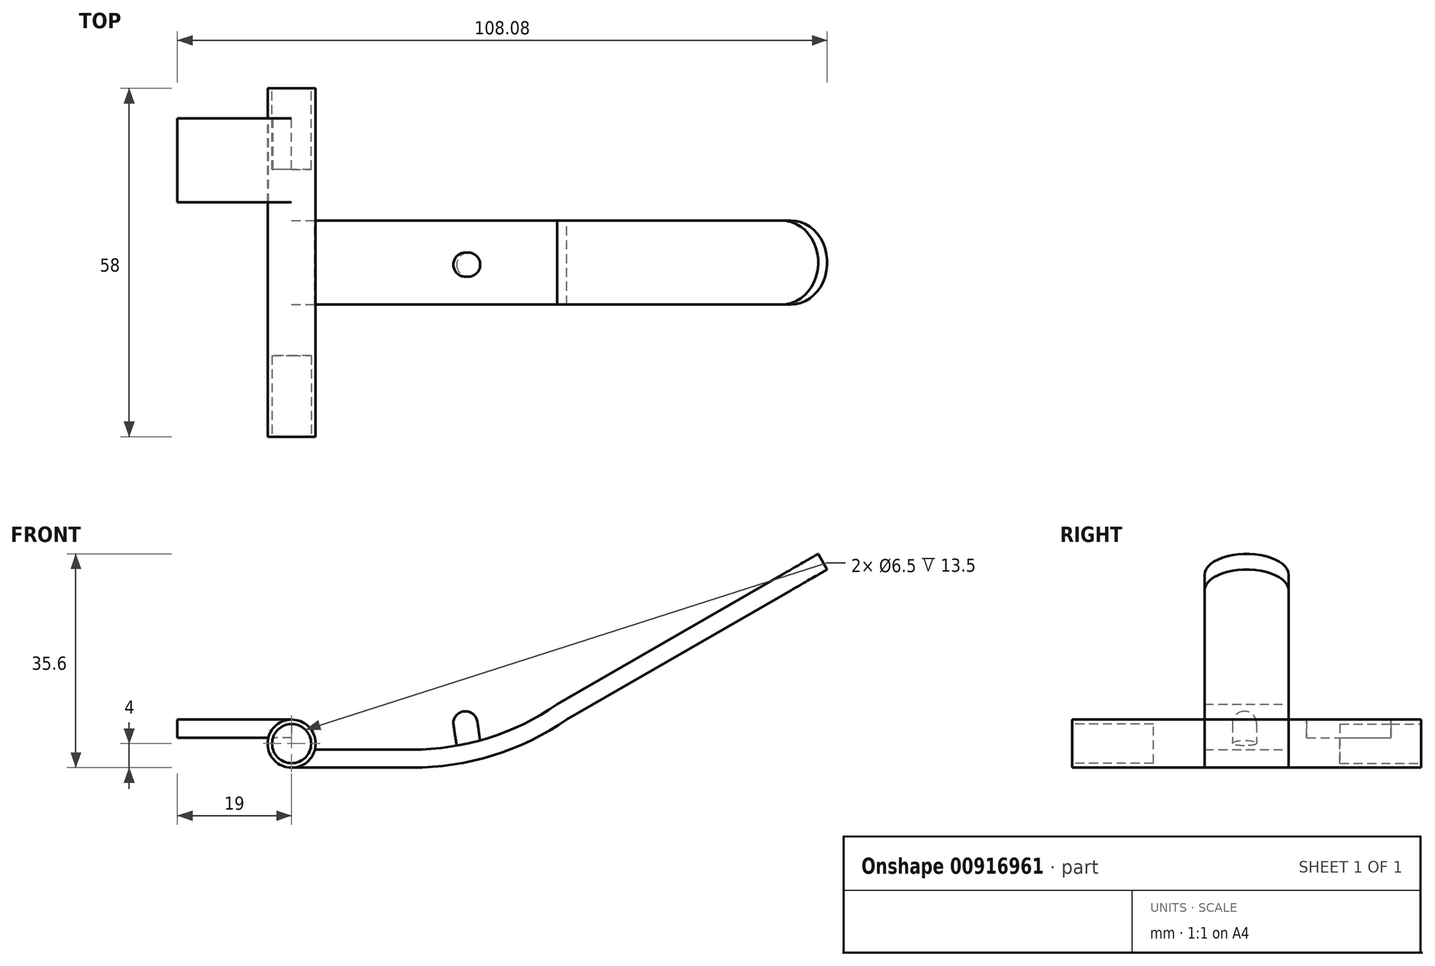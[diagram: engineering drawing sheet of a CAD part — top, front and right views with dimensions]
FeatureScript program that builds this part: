
annotation { "Feature Type Name" : "Feature", "Feature Type Description" : "" }
export const myFeature = defineFeature(function(context is Context, id is Id, definition is map)
    precondition{}
    {
        {
            var Q0;
            Q0=qCreatedBy(makeId("Front.planeOp"),FACE);
            var sketch = newSketch(context, id + "F0", { "sketchPlane" : qUnion([Q0])});
            skCircle(sketch, "E0", {"center": v(0, 0) * mm, "radius": 4 * mm});
            skSolve(sketch);
        }
        {
            var Q0;
            Q0=makeQuery(id+"F0.imprint","IMPRINT",FACE,{"disambiguationData":[TD([[makeQuery(id+"F0.imprint","IMPRINT",EDGE,{"derivedFrom":sQuery(id+"F0.wireOp",EDGE,"E0")}),1.0]])]});
            extrude(context, id + "F1", {"entities" : qUnion([Q0]), "depth" : 58 * mm, "offsetDistance" : 25 * mm});
        }
        {
            var Q0;
            Q0=makeQuery(id+"F1.opExtrude","CAP_FACE",FACE,{"disambiguationData":[OSD([sQuery(id+"F0.wireOp",EDGE,"E0")])],"isStart":false});
            var sketch = newSketch(context, id + "F2", { "sketchPlane" : qUnion([Q0])});
            skCircle(sketch, "E1", {"center": v(0, 0) * mm, "radius": 3.25 * mm});
            skSolve(sketch);
        }
        {
            var Q0;
            Q0=makeQuery(id+"F2.imprint","IMPRINT",FACE,{"disambiguationData":[TD([[makeQuery(id+"F2.imprint","IMPRINT",EDGE,{"derivedFrom":sQuery(id+"F2.wireOp",EDGE,"E1")}),1.0]])]});
            extrude(context, id + "F3", {"entities" : qUnion([Q0]), "operationType" : NewBodyOperationType.REMOVE, "oppositeDirection" : true, "depth" : 13.5 * mm, "offsetDistance" : 25 * mm});
        }
        {
            var Q0;
            Q0=makeQuery(id+"F1.opExtrude","CAP_FACE",FACE,{"disambiguationData":[OSD([sQuery(id+"F0.wireOp",EDGE,"E0")])],"isStart":true});
            var sketch = newSketch(context, id + "F4", { "sketchPlane" : qUnion([Q0])});
            skCircle(sketch, "E2", {"center": v(0, 0) * mm, "radius": 3.25 * mm});
            skSolve(sketch);
        }
        {
            var Q0;
            Q0=makeQuery(id+"F4.imprint","IMPRINT",FACE,{"disambiguationData":[TD([[makeQuery(id+"F4.imprint","IMPRINT",EDGE,{"derivedFrom":sQuery(id+"F4.wireOp",EDGE,"E2")}),1.0]])]});
            extrude(context, id + "F5", {"entities" : qUnion([Q0]), "operationType" : NewBodyOperationType.REMOVE, "oppositeDirection" : true, "depth" : 13.5 * mm, "offsetDistance" : 25 * mm});
        }
        {
            var Q0;
            Q0=makeQuery(id+"F1.opExtrude","CAP_FACE",FACE,{"disambiguationData":[OSD([sQuery(id+"F0.wireOp",EDGE,"E0")])],"isStart":false});
            cPlane(context, id + "F6", {"entities" : qUnion([Q0]), "cplaneType" : CPlaneType.OFFSET, "offset" : 29 * mm, "oppositeDirection" : true, "width" : 150 * mm, "height" : 150 * mm});
        }
        {
            var Q0;
            Q0=qCreatedBy(id+"F6.planeOp",FACE);
            var sketch = newSketch(context, id + "F7", { "sketchPlane" : qUnion([Q0])});
            skLineSegment(sketch, "E3", {"start": v(0, -4) * mm, "end": v(20, -4) * mm});
            skLineSegment(sketch, "E4", {"start": v(45.78, 4) * mm, "end": v(89.08, 29) * mm});
            skArc(sketch, "E5", {"start": v(20, -4) * mm, "mid": v(33.5, -1.95) * mm, "end": v(45.78, 4) * mm});
            skLineSegment(sketch, "E6.0", {"start": v(0, -1) * mm, "end": v(20, -1) * mm});
            skArc(sketch, "E7.0", {"start": v(20, -1) * mm, "mid": v(32.66, 0.93) * mm, "end": v(44.18, 6.54) * mm});
            skLineSegment(sketch, "E8.0", {"start": v(44.18, 6.54) * mm, "end": v(87.58, 31.6) * mm});
            skLineSegment(sketch, "E9", {"start": v(89.08, 29) * mm, "end": v(87.58, 31.6) * mm});
            skLineSegment(sketch, "E10", {"start": v(0, -1) * mm, "end": v(0, -4) * mm});
            skSolve(sketch);
        }
        {
            var Q0;
            Q0 = qSketchRegion(id + "F7", true);
            extrude(context, id + "F8", {"entities" : qUnion([Q0]), "operationType" : NewBodyOperationType.ADD, "depth" : 7 * mm, "offsetDistance" : 25 * mm, "hasSecondDirection" : true, "secondDirectionOppositeDirection" : true, "secondDirectionDepth" : 7 * mm});
        }
        {
            var Q0;
            Q0=makeQuery(id+"F8.opExtrude","CAP_EDGE",EDGE,{"disambiguationData":[OSD([sQuery(id+"F7.wireOp",EDGE,"E9")])],"isStart":false});
            var Q1;
            Q1=makeQuery(id+"F8.opExtrude","CAP_EDGE",EDGE,{"disambiguationData":[OSD([sQuery(id+"F7.wireOp",EDGE,"E9")])],"isStart":true});
            fillet(context, id + "F9", {"entities" : qUnion([Q0, Q1]), "radius" : 7 * mm, "tangentPropagation" : true, "allowEdgeOverflow" : false});
        }
        {
            var Q0;
            Q0=makeQuery(id+"F1.opExtrude","CAP_FACE",FACE,{"disambiguationData":[OSD([sQuery(id+"F0.wireOp",EDGE,"E0")])],"isStart":true});
            cPlane(context, id + "F10", {"entities" : qUnion([Q0]), "cplaneType" : CPlaneType.OFFSET, "offset" : 5 * mm, "oppositeDirection" : true, "width" : 150 * mm, "height" : 150 * mm});
        }
        {
            var Q0;
            Q0=qCreatedBy(id+"F10.planeOp",FACE);
            var sketch = newSketch(context, id + "F11", { "sketchPlane" : qUnion([Q0])});
            skLineSegment(sketch, "E11.bottom", {"start": v(0, 4) * mm, "end": v(19, 4) * mm});
            skLineSegment(sketch, "E11.top", {"start": v(0, 1) * mm, "end": v(19, 1) * mm});
            skLineSegment(sketch, "E11.left", {"start": v(0, 4) * mm, "end": v(0, 1) * mm});
            skLineSegment(sketch, "E11.right", {"start": v(19, 4) * mm, "end": v(19, 1) * mm});
            skSolve(sketch);
        }
        {
            var Q0;
            Q0=makeQuery(id+"F11.imprint","IMPRINT",FACE,{"disambiguationData":[TD([[makeQuery(id+"F11.imprint","IMPRINT",EDGE,{"derivedFrom":sQuery(id+"F11.wireOp",EDGE,"E11.bottom")}),-1.0]])]});
            extrude(context, id + "F12", {"entities" : qUnion([Q0]), "operationType" : NewBodyOperationType.ADD, "oppositeDirection" : true, "depth" : 14 * mm, "offsetDistance" : 25 * mm});
        }
        {
            var Q0;
            Q0=makeQuery(id+"F8.opExtrude","CAP_EDGE",EDGE,{"disambiguationData":[OSD([sQuery(id+"F7.wireOp",EDGE,"E7.0")])],"isStart":true});
            cPoint(context, id + "F13", {"entities" : qUnion([Q0]), "parameter" : 0.5});
        }
        {
            var Q0;
            Q0=makeQuery(id+"F8.opExtrude","CAP_EDGE",EDGE,{"disambiguationData":[OSD([sQuery(id+"F7.wireOp",EDGE,"E7.0")])],"isStart":false});
            cPoint(context, id + "F14", {"entities" : qUnion([Q0]), "parameter" : 0.5});
        }
        {
            var Q0;
            Q0=makeQuery(id+"F8.opExtrude","SWEPT_EDGE",EDGE,{"disambiguationData":[OSD([sQuery(id+"F7.wireOp",EDGE,"E6.0"),sQuery(id+"F7.wireOp",EDGE,"E7.0")])]});
            cPoint(context, id + "F15", {"entities" : qUnion([Q0]), "parameter" : 0.5});
        }
        {
            var Q0;
            Q0 = qCreatedBy(id + "F13" ,VERTEX);
            var Q1;
            Q1 = qCreatedBy(id + "F14" ,VERTEX);
            var Q2;
            Q2 = qCreatedBy(id + "F15" ,VERTEX);
            cPlane(context, id + "F16", {"entities" : qUnion([Q0, Q1, Q2]), "cplaneType" : CPlaneType.THREE_POINT, "offset" : 25 * mm, "width" : 150 * mm, "height" : 150 * mm});
        }
        {
            var Q0;
            Q0=qCreatedBy(id+"F16.planeOp",FACE);
            var sketch = newSketch(context, id + "F17", { "sketchPlane" : qUnion([Q0])});
            skCircle(sketch, "E12", {"center": v(29.08, -29.35) * mm, "radius": 2 * mm});
            skSolve(sketch);
        }
        {
            var Q0;
            Q0=makeQuery(id+"F17.imprint","IMPRINT",FACE,{"disambiguationData":[TD([[makeQuery(id+"F17.imprint","IMPRINT",EDGE,{"derivedFrom":sQuery(id+"F17.wireOp",EDGE,"E12")}),1.0]])]});
            extrude(context, id + "F18", {"entities" : qUnion([Q0]), "operationType" : NewBodyOperationType.ADD, "depth" : 5 * mm, "offsetDistance" : 25 * mm, "hasSecondDirection" : true, "secondDirectionBound" : BoundingType.UP_TO_NEXT, "secondDirectionOppositeDirection" : true, "secondDirectionDepth" : 25 * mm});
        }
        {
            var Q0;
            {var subQ0=sQuery(id+"F17.wireOp",EDGE,"E12");Q0=makeQuery(id+"F18.opExtrude","CAP_EDGE",EDGE,{"disambiguationData":[OSD([subQ0]),topologyDisambiguationEdgeConnected([makeQuery(id+"F17.imprint","IMPRINT",EDGE,{"derivedFrom":subQ0})])],"isStart":false});}
            fillet(context, id + "F19", {"entities" : qUnion([Q0]), "radius" : 2 * mm, "tangentPropagation" : true, "allowEdgeOverflow" : false});
        }
    });
